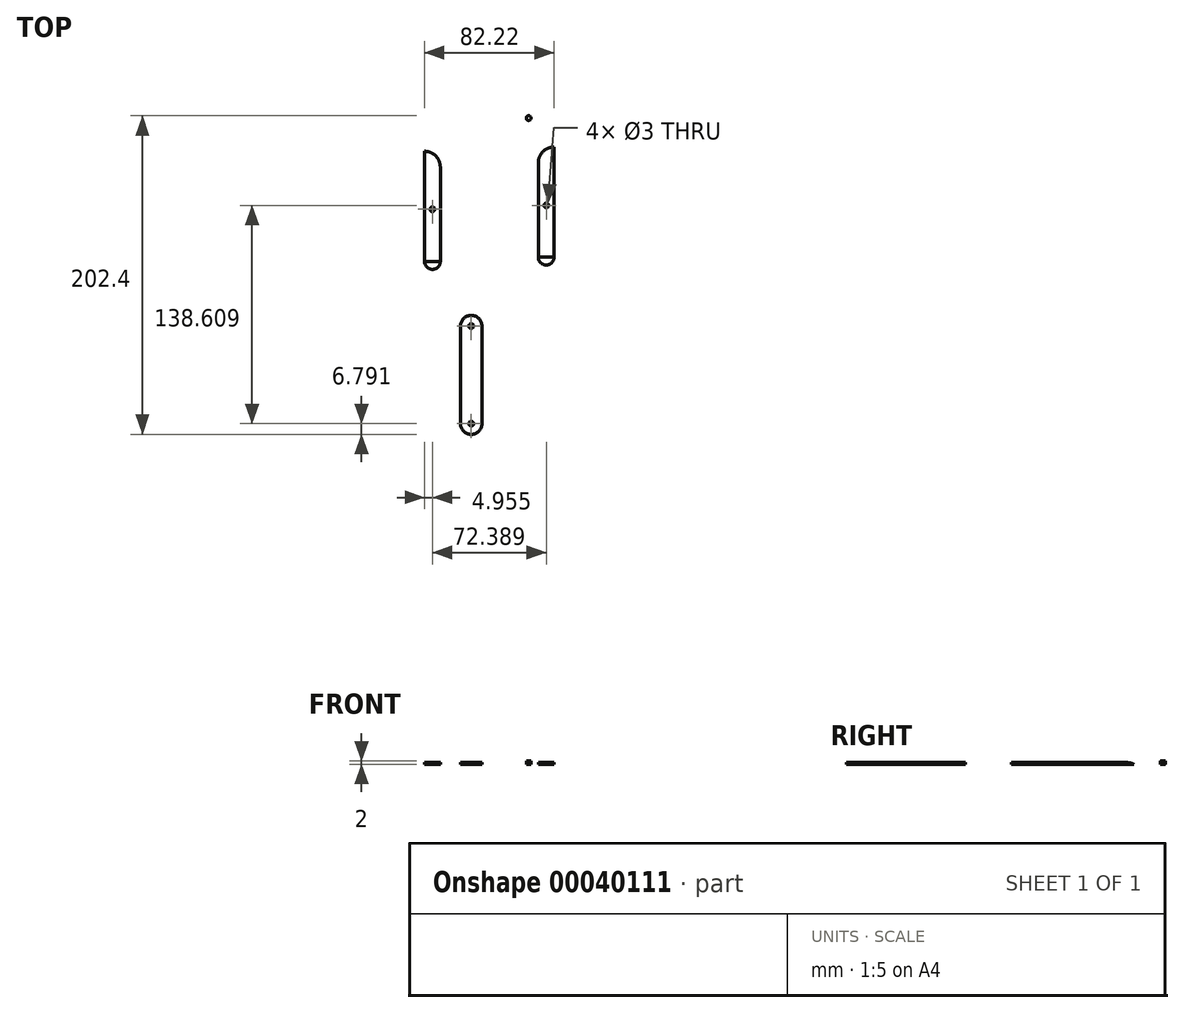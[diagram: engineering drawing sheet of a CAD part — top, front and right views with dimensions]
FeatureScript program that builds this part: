
annotation { "Feature Type Name" : "Feature", "Feature Type Description" : "" }
export const myFeature = defineFeature(function(context is Context, id is Id, definition is map)
    precondition{}
    {
        {
            var Q0;
            Q0=qCreatedBy(makeId("Top.planeOp"),FACE);
            var sketch = newSketch(context, id + "F0", { "sketchPlane" : qUnion([Q0])});
            skLineSegment(sketch, "E0.bottom", {"start": v(-43.6, 34.4) * mm, "end": v(-33.6, 34.4) * mm});
            skLineSegment(sketch, "E0.top", {"start": v(-43.6, -35.6) * mm, "end": v(-33.6, -35.6) * mm});
            skLineSegment(sketch, "E0.left", {"start": v(-43.6, 34.4) * mm, "end": v(-43.6, -35.6) * mm});
            skLineSegment(sketch, "E0.right", {"start": v(-33.6, 34.4) * mm, "end": v(-33.6, -35.6) * mm});
            skLineSegment(sketch, "E1.bottom", {"start": v(11.67, -29.74) * mm, "end": v(81.67, -29.74) * mm});
            skLineSegment(sketch, "E1.top", {"start": v(11.67, -39.74) * mm, "end": v(81.67, -39.74) * mm});
            skLineSegment(sketch, "E1.left", {"start": v(11.67, -29.74) * mm, "end": v(11.67, -39.74) * mm});
            skLineSegment(sketch, "E1.right", {"start": v(81.67, -29.74) * mm, "end": v(81.67, -39.74) * mm});
            skSolve(sketch);
        }
        {
            var Q0;
            Q0=makeQuery(id+"F0.imprint","IMPRINT",FACE,{"disambiguationData":[TD([[makeQuery(id+"F0.imprint","IMPRINT",EDGE,{"derivedFrom":sQuery(id+"F0.wireOp",EDGE,"E0.bottom")}),-1.0]])]});
            extrude(context, id + "F1", {"entities" : qUnion([Q0]), "depth" : 1 * mm});
        }
        {
            var Q0;
            Q0=makeQuery(id+"F1.opExtrude","SWEPT_EDGE",EDGE,{"disambiguationData":[OSD([sQuery(id+"F0.wireOp",EDGE,"E0.bottom"),sQuery(id+"F0.wireOp",EDGE,"E0.right")])]});
            var Q1;
            Q1=makeQuery(id+"F1.opExtrude","CAP_EDGE",EDGE,{"disambiguationData":[OSD([sQuery(id+"F0.wireOp",EDGE,"E0.bottom")])],"isStart":false});
            fillet(context, id + "F2", {"entities" : qUnion([Q0, Q1]), "radius" : 10 * mm, "tangentPropagation" : true, "allowEdgeOverflow" : false});
        }
        {
            var Q0;
            Q0=qCreatedBy(makeId("Top.planeOp"),FACE);
            var sketch = newSketch(context, id + "F3", { "sketchPlane" : qUnion([Q0])});
            skLineSegment(sketch, "E2.bottom", {"start": v(28.62, 37.1) * mm, "end": v(38.62, 37.1) * mm});
            skLineSegment(sketch, "E2.top", {"start": v(28.62, -32.9) * mm, "end": v(38.62, -32.9) * mm});
            skLineSegment(sketch, "E2.left", {"start": v(28.62, 37.1) * mm, "end": v(28.62, -32.9) * mm});
            skLineSegment(sketch, "E2.right", {"start": v(38.62, 37.1) * mm, "end": v(38.62, -32.9) * mm});
            skSolve(sketch);
        }
        {
            var Q0;
            Q0=makeQuery(id+"F3.imprint","IMPRINT",FACE,{"disambiguationData":[TD([[makeQuery(id+"F3.imprint","IMPRINT",EDGE,{"derivedFrom":sQuery(id+"F3.wireOp",EDGE,"E2.bottom")}),-1.0]])]});
            extrude(context, id + "F4", {"entities" : qUnion([Q0]), "depth" : 1 * mm});
        }
        {
            var Q0;
            Q0=makeQuery(id+"F4.opExtrude","SWEPT_EDGE",EDGE,{"disambiguationData":[OSD([sQuery(id+"F3.wireOp",EDGE,"E2.bottom"),sQuery(id+"F3.wireOp",EDGE,"E2.left")])]});
            var Q1;
            Q1=makeQuery(id+"F4.opExtrude","CAP_EDGE",EDGE,{"disambiguationData":[OSD([sQuery(id+"F3.wireOp",EDGE,"E2.bottom")])],"isStart":false});
            fillet(context, id + "F5", {"entities" : qUnion([Q0, Q1]), "radius" : 10 * mm, "tangentPropagation" : true, "allowEdgeOverflow" : false});
        }
        {
            var Q0;
            Q0=makeQuery(id+"F4.opExtrude","CAP_FACE",FACE,{"disambiguationData":[OSD([sQuery(id+"F3.wireOp",EDGE,"E2.bottom"),sQuery(id+"F3.wireOp",EDGE,"E2.top"),sQuery(id+"F3.wireOp",EDGE,"E2.left"),sQuery(id+"F3.wireOp",EDGE,"E2.right")])],"isStart":false});
            var sketch = newSketch(context, id + "F6", { "sketchPlane" : qUnion([Q0])});
            skPoint(sketch, "E3", {"position": v(33.74, 0) * mm});
            skPoint(sketch, "E4", {"position": v(-38.98, 0) * mm});
            skArc(sketch, "E5", {"start": v(28.62, -32.9) * mm, "mid": v(33.62, -37.9) * mm, "end": v(38.62, -32.9) * mm});
            skSolve(sketch);
        }
        {
            var Q0;
            Q0=sQuery(id+"F6.wireOp",VERTEX,"E3");
            var Q1;
            Q1=makeQuery(id+"F4.opExtrude","SWEPT_BODY",BODY,{"disambiguationData":[OSD([sQuery(id+"F3.wireOp",EDGE,"E2.bottom"),sQuery(id+"F3.wireOp",EDGE,"E2.top"),sQuery(id+"F3.wireOp",EDGE,"E2.left"),sQuery(id+"F3.wireOp",EDGE,"E2.right")])]});
            hole(context, id + "F7", {"style" : HoleStyle.SIMPLE, "holeDiameter" : 3 * mm, "endStyle" : HoleEndStyle.THROUGH, "locations" : qUnion([Q0]), "scope" : qUnion([Q1])});
        }
        {
            var Q0;
            Q0=makeQuery(id+"F1.opExtrude","CAP_FACE",FACE,{"disambiguationData":[OSD([sQuery(id+"F0.wireOp",EDGE,"E0.bottom"),sQuery(id+"F0.wireOp",EDGE,"E0.top"),sQuery(id+"F0.wireOp",EDGE,"E0.left"),sQuery(id+"F0.wireOp",EDGE,"E0.right")])],"isStart":false});
            var sketch = newSketch(context, id + "F8", { "sketchPlane" : qUnion([Q0])});
            skLineSegment(sketch, "E6", {"start": v(-33.6, -35.6) * mm, "end": v(-33.6, -2.62) * mm});
            skArc(sketch, "E7", {"start": v(-43.6, -35.6) * mm, "mid": v(-38.6, -40.6) * mm, "end": v(-33.6, -35.6) * mm});
            skSolve(sketch);
        }
        {
            var Q0;
            {var subQ2=sQuery(id+"F8.wireOp",EDGE,"E6");Q0=makeQuery(id+"F8.imprint","IMPRINT",FACE,{"disambiguationData":[TD([[makeQuery(id+"F8.imprint","IMPRINT",EDGE,{"derivedFrom":subQ2}),-1.0]])]});}
            var sketch = newSketch(context, id + "F9", { "sketchPlane" : qUnion([Q0])});
            skLineSegment(sketch, "E8", {"start": v(-33.67, -2.43) * mm, "end": v(-43.62, -2.43) * mm});
            skPoint(sketch, "E9", {"position": v(-38.65, -2.43) * mm});
            skSolve(sketch);
        }
        {
            var Q0;
            Q0=sQuery(id+"F9.wireOp",VERTEX,"E9");
            var Q1;
            Q1=makeQuery(id+"F1.opExtrude","SWEPT_BODY",BODY,{"disambiguationData":[OSD([sQuery(id+"F0.wireOp",EDGE,"E0.bottom"),sQuery(id+"F0.wireOp",EDGE,"E0.top"),sQuery(id+"F0.wireOp",EDGE,"E0.left"),sQuery(id+"F0.wireOp",EDGE,"E0.right")])]});
            hole(context, id + "F10", {"style" : HoleStyle.SIMPLE, "holeDiameter" : 3 * mm, "endStyle" : HoleEndStyle.THROUGH, "locations" : qUnion([Q0]), "scope" : qUnion([Q1])});
        }
        {
            var Q0;
            Q0=qCreatedBy(makeId("Top.planeOp"),FACE);
            var sketch = newSketch(context, id + "F11", { "sketchPlane" : qUnion([Q0])});
            skCircle(sketch, "E10", {"center": v(-23.26, 47.93) * mm, "radius": 1.5 * mm});
            skCircle(sketch, "E11", {"center": v(22.51, 55.5) * mm, "radius": 1.5 * mm});
            skSolve(sketch);
        }
        {
            var Q0;
            Q0=makeQuery(id+"F11.imprint","IMPRINT",FACE,{"disambiguationData":[TD([[makeQuery(id+"F11.imprint","IMPRINT",EDGE,{"derivedFrom":sQuery(id+"F11.wireOp",EDGE,"E11")}),1.0]])]});
            extrude(context, id + "F12", {"entities" : qUnion([Q0]), "depth" : 2 * mm});
        }
        {
            var Q0;
            Q0=qCreatedBy(makeId("Top.planeOp"),FACE);
            var sketch = newSketch(context, id + "F13", { "sketchPlane" : qUnion([Q0])});
            skLineSegment(sketch, "E12", {"start": v(-20.76, -76.6) * mm, "end": v(-20.76, -138.6) * mm});
            skArc(sketch, "E13", {"start": v(-7.18, -76.6) * mm, "mid": v(-13.97, -69.82) * mm, "end": v(-20.76, -76.6) * mm});
            skArc(sketch, "E14", {"start": v(-20.76, -138.6) * mm, "mid": v(-13.97, -145.4) * mm, "end": v(-7.18, -138.6) * mm});
            skPoint(sketch, "E15.end.orphan", {"position": v(-7.18, -135.21) * mm});
            skLineSegment(sketch, "E16", {"start": v(-7.18, -76.6) * mm, "end": v(-7.18, -138.6) * mm});
            skPoint(sketch, "E17", {"position": v(5.26, -71.28) * mm});
            skCircle(sketch, "E18", {"center": v(-13.97, -76.6) * mm, "radius": 1.5 * mm});
            skCircle(sketch, "E19", {"center": v(-13.97, -138.6) * mm, "radius": 1.5 * mm});
            skSolve(sketch);
        }
        {
            var Q0;
            Q0=makeQuery(id+"F13.imprint","IMPRINT",FACE,{"disambiguationData":[TD([[makeQuery(id+"F13.imprint","IMPRINT",EDGE,{"derivedFrom":sQuery(id+"F13.wireOp",EDGE,"E12")}),1.0]])]});
            extrude(context, id + "F14", {"entities" : qUnion([Q0]), "depth" : 1 * mm});
        }
        {
            var Q0;
            Q0=makeQuery(id+"F6.imprint","IMPRINT",FACE,{"disambiguationData":[TD([[makeQuery(id+"F6.imprint","IMPRINT",EDGE,{"derivedFrom":sQuery(id+"F6.wireOp",EDGE,"E5")}),1.0]])]});
            extrude(context, id + "F15", {"entities" : qUnion([Q0]), "oppositeDirection" : true, "depth" : 1 * mm});
        }
        {
            var Q0;
            Q0=makeQuery(id+"F8.imprint","IMPRINT",FACE,{"disambiguationData":[TD([[makeQuery(id+"F8.imprint","IMPRINT",EDGE,{"derivedFrom":sQuery(id+"F8.wireOp",EDGE,"E7")}),1.0]])]});
            extrude(context, id + "F16", {"entities" : qUnion([Q0]), "oppositeDirection" : true, "depth" : 1 * mm});
        }
    });
